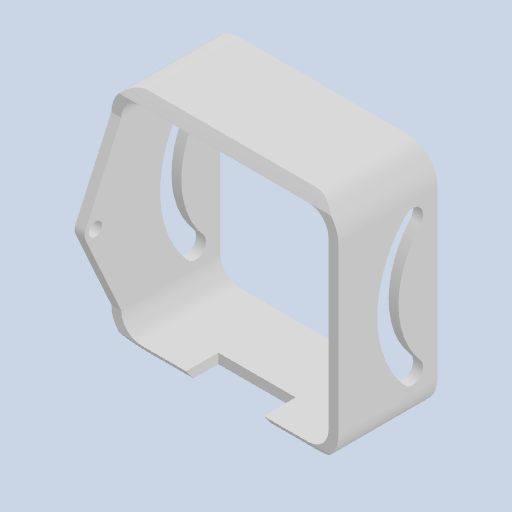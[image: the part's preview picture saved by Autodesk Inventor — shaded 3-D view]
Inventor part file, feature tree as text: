
AUTODESK INVENTOR PART (.ipt)
format: ipt  version: 2022 (Build 260153000, 153)  size: 227,328 bytes
history: native  units: mm
features: reference x9, other x8, extrude x5, sketch x5
ambient origin geometry x8: Origin, YZ Plane, XZ Plane, XY Plane, X Axis, Y Axis, Z Axis, Center Point
bodies: Body1 (feature_tree)
feature tree (27):
  other  "Твердое тело1"
  other  "РабПлоскость1"
  extrude  "Выдавливание1"  Depth=7.0mm
  extrude  "Выдавливание2"  Depth=7.0mm
  extrude  "Выдавливание3"  Depth=7.0mm
  extrude  "Выдавливание5"  Depth=7.0mm
  sketch  "Эскиз6"
  other  "РабПлоскость2"
  extrude  "Выдавливание6"  Depth=0.2mm
  sketch  "Эскиз1"
  reference  "Ссылка1"
  reference  "Ссылка2"
  sketch  "Эскиз2"
  sketch  "Эскиз3"
  reference  "Ссылка3"
  reference  "Ссылка4"
  reference  "Ссылка5"
  sketch  "Эскиз5"
  reference  "Ссылка7"
  reference  "Ссылка8"
  reference  "Ссылка9"
  reference  "Ссылка10"
  other  "<userpath>\Documents\Git\MZCAT_2024\MZCAT_2.iam"
  other  "MZCAT_2.iam"
  other  "LD19:1"
  other  "stabilisator_plan:1"
  other  "lidar_krestovina:1"
